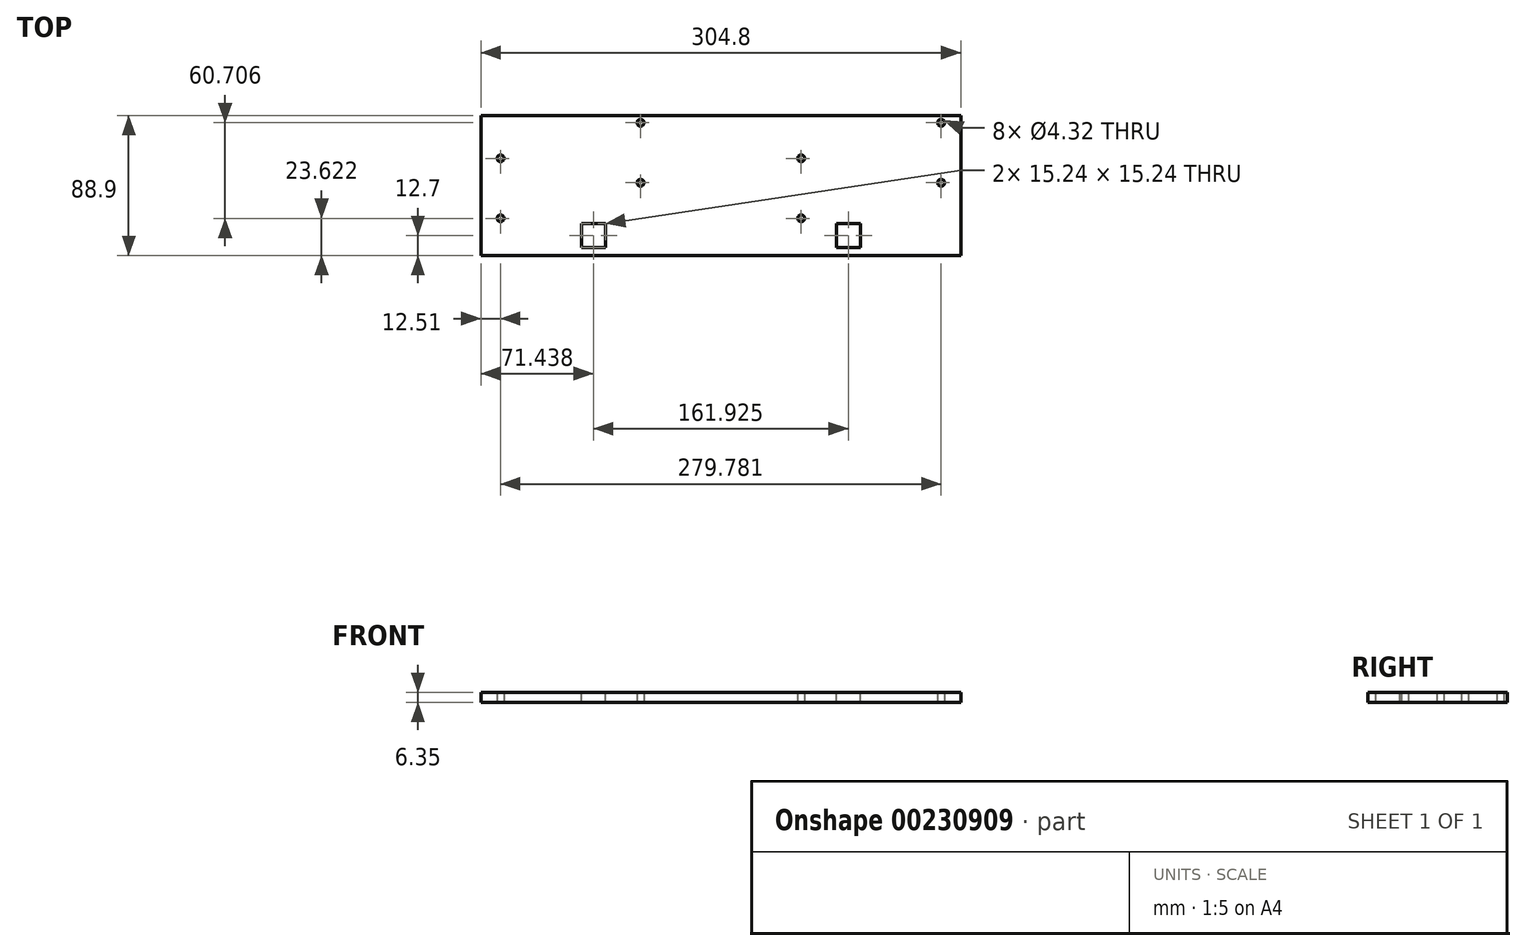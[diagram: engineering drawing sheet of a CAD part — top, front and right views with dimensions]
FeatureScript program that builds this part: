
annotation { "Feature Type Name" : "Feature", "Feature Type Description" : "" }
export const myFeature = defineFeature(function(context is Context, id is Id, definition is map)
    precondition{}
    {
        {
            var Q0;
            Q0=qCreatedBy(makeId("Top.planeOp"),FACE);
            var sketch = newSketch(context, id + "F0", { "sketchPlane" : qUnion([Q0])});
            skLineSegment(sketch, "E0.bottom", {"start": v(152.4, -44.45) * mm, "end": v(-152.4, -44.45) * mm});
            skLineSegment(sketch, "E0.top", {"start": v(152.4, 44.45) * mm, "end": v(-152.4, 44.45) * mm});
            skLineSegment(sketch, "E0.left", {"start": v(152.4, -44.45) * mm, "end": v(152.4, 44.45) * mm});
            skLineSegment(sketch, "E0.right", {"start": v(-152.4, -44.45) * mm, "end": v(-152.4, 44.45) * mm});
            skPoint(sketch, "E0.middle", {"position": v(0, 0) * mm});
            skSolve(sketch);
        }
        {
            var Q0;
            Q0 = qSketchRegion(id + "F0", true);
            extrude(context, id + "F1", {"entities" : qUnion([Q0]), "oppositeDirection" : true, "depth" : 6.35 * mm});
        }
        {
            var Q0;
            Q0=makeQuery(id+"F1.opExtrude","CAP_FACE",FACE,{"disambiguationData":[OSD([sQuery(id+"F0.wireOp",EDGE,"E0.bottom"),sQuery(id+"F0.wireOp",EDGE,"E0.top"),sQuery(id+"F0.wireOp",EDGE,"E0.left"),sQuery(id+"F0.wireOp",EDGE,"E0.right")])],"isStart":true});
            var sketch = newSketch(context, id + "F2", { "sketchPlane" : qUnion([Q0])});
            skLineSegment(sketch, "E1", {"start": v(0, 44.45) * mm, "end": v(0, -44.45) * mm, "construction": true});
            skLineSegment(sketch, "E2", {"start": v(-152.4, -31.75) * mm, "end": v(152.4, -31.75) * mm, "construction": true});
            skLineSegment(sketch, "E3.bottom", {"start": v(-73.34, -39.37) * mm, "end": v(-88.58, -39.37) * mm});
            skLineSegment(sketch, "E3.top", {"start": v(-73.34, -24.13) * mm, "end": v(-88.58, -24.13) * mm});
            skLineSegment(sketch, "E3.left", {"start": v(-73.34, -39.37) * mm, "end": v(-73.34, -24.13) * mm});
            skLineSegment(sketch, "E3.right", {"start": v(-88.58, -39.37) * mm, "end": v(-88.58, -24.13) * mm});
            skPoint(sketch, "E3.middle", {"position": v(-80.96, -31.75) * mm});
            skLineSegment(sketch, "E4.bottom", {"start": v(88.58, -39.37) * mm, "end": v(73.34, -39.37) * mm});
            skLineSegment(sketch, "E4.top", {"start": v(88.58, -24.13) * mm, "end": v(73.34, -24.13) * mm});
            skLineSegment(sketch, "E4.left", {"start": v(88.58, -39.37) * mm, "end": v(88.58, -24.13) * mm});
            skLineSegment(sketch, "E4.right", {"start": v(73.34, -39.37) * mm, "end": v(73.34, -24.13) * mm});
            skPoint(sketch, "E4.middle", {"position": v(80.96, -31.75) * mm});
            skSolve(sketch);
        }
        {
            var Q0;
            Q0 = qSketchRegion(id + "F2", true);
            extrude(context, id + "F3", {"entities" : qUnion([Q0]), "operationType" : NewBodyOperationType.REMOVE, "oppositeDirection" : true, "depth" : 25.4 * mm});
        }
        {
            var Q0;
            Q0=makeQuery(id+"F1.opExtrude","CAP_FACE",FACE,{"disambiguationData":[OSD([sQuery(id+"F0.wireOp",EDGE,"E0.bottom"),sQuery(id+"F0.wireOp",EDGE,"E0.top"),sQuery(id+"F0.wireOp",EDGE,"E0.left"),sQuery(id+"F0.wireOp",EDGE,"E0.right")])],"isStart":true});
            var sketch = newSketch(context, id + "F4", { "sketchPlane" : qUnion([Q0])});
            skLineSegment(sketch, "E5", {"start": v(0, 44.45) * mm, "end": v(0, -44.45) * mm, "construction": true});
            skLineSegment(sketch, "E6", {"start": v(-152.4, 17.27) * mm, "end": v(152.4, 17.27) * mm, "construction": true});
            skLineSegment(sketch, "E7", {"start": v(-152.4, 39.88) * mm, "end": v(152.4, 39.88) * mm, "construction": true});
            skLineSegment(sketch, "E8", {"start": v(152.4, 1.78) * mm, "end": v(-152.4, 1.78) * mm, "construction": true});
            skLineSegment(sketch, "E9", {"start": v(-152.4, -20.83) * mm, "end": v(152.4, -20.83) * mm, "construction": true});
            skPoint(sketch, "E10", {"position": v(-51, 39.88) * mm});
            skPoint(sketch, "E11", {"position": v(139.9, 39.88) * mm});
            skPoint(sketch, "E12", {"position": v(-139.9, 17.27) * mm});
            skPoint(sketch, "E13", {"position": v(51, 17.27) * mm});
            skPoint(sketch, "E14", {"position": v(51, -20.83) * mm});
            skPoint(sketch, "E15", {"position": v(139.9, 1.78) * mm});
            skPoint(sketch, "E16", {"position": v(-139.9, -20.83) * mm});
            skPoint(sketch, "E17", {"position": v(-51, 1.78) * mm});
            skSolve(sketch);
        }
        {
            var Q0;
            Q0=sQuery(id+"F4.wireOp",VERTEX,"E10");
            var Q1;
            Q1=sQuery(id+"F4.wireOp",VERTEX,"E12");
            var Q2;
            Q2=sQuery(id+"F4.wireOp",VERTEX,"E17");
            var Q3;
            Q3=sQuery(id+"F4.wireOp",VERTEX,"E16");
            var Q4;
            Q4=sQuery(id+"F4.wireOp",VERTEX,"E15");
            var Q5;
            Q5=sQuery(id+"F4.wireOp",VERTEX,"E11");
            var Q6;
            Q6=sQuery(id+"F4.wireOp",VERTEX,"E13");
            var Q7;
            Q7=sQuery(id+"F4.wireOp",VERTEX,"E14");
            var Q8;
            Q8=makeQuery(id+"F1.opExtrude","SWEPT_BODY",BODY,{"disambiguationData":[OSD([sQuery(id+"F0.wireOp",EDGE,"E0.bottom"),sQuery(id+"F0.wireOp",EDGE,"E0.top"),sQuery(id+"F0.wireOp",EDGE,"E0.left"),sQuery(id+"F0.wireOp",EDGE,"E0.right")])]});
            hole(context, id + "F5", {"style" : HoleStyle.SIMPLE, "endStyle" : HoleEndStyle.THROUGH, "standardTappedOrClearance" : lookupTablePath({ "standard" : "ANSI", "fit" : "Close", "size" : "#8", "type" : "Clearance" }), "standardBlindInLast" : lookupTablePath({ "fit" : "Close", "standard" : "ANSI", "size" : "#8", "type" : "Clearance" }), "holeDiameter" : 4.32 * mm, "locations" : qUnion([Q0, Q1, Q2, Q3, Q4, Q5, Q6, Q7]), "scope" : qUnion([Q8]), "isTappedThrough" : true});
        }
    });
